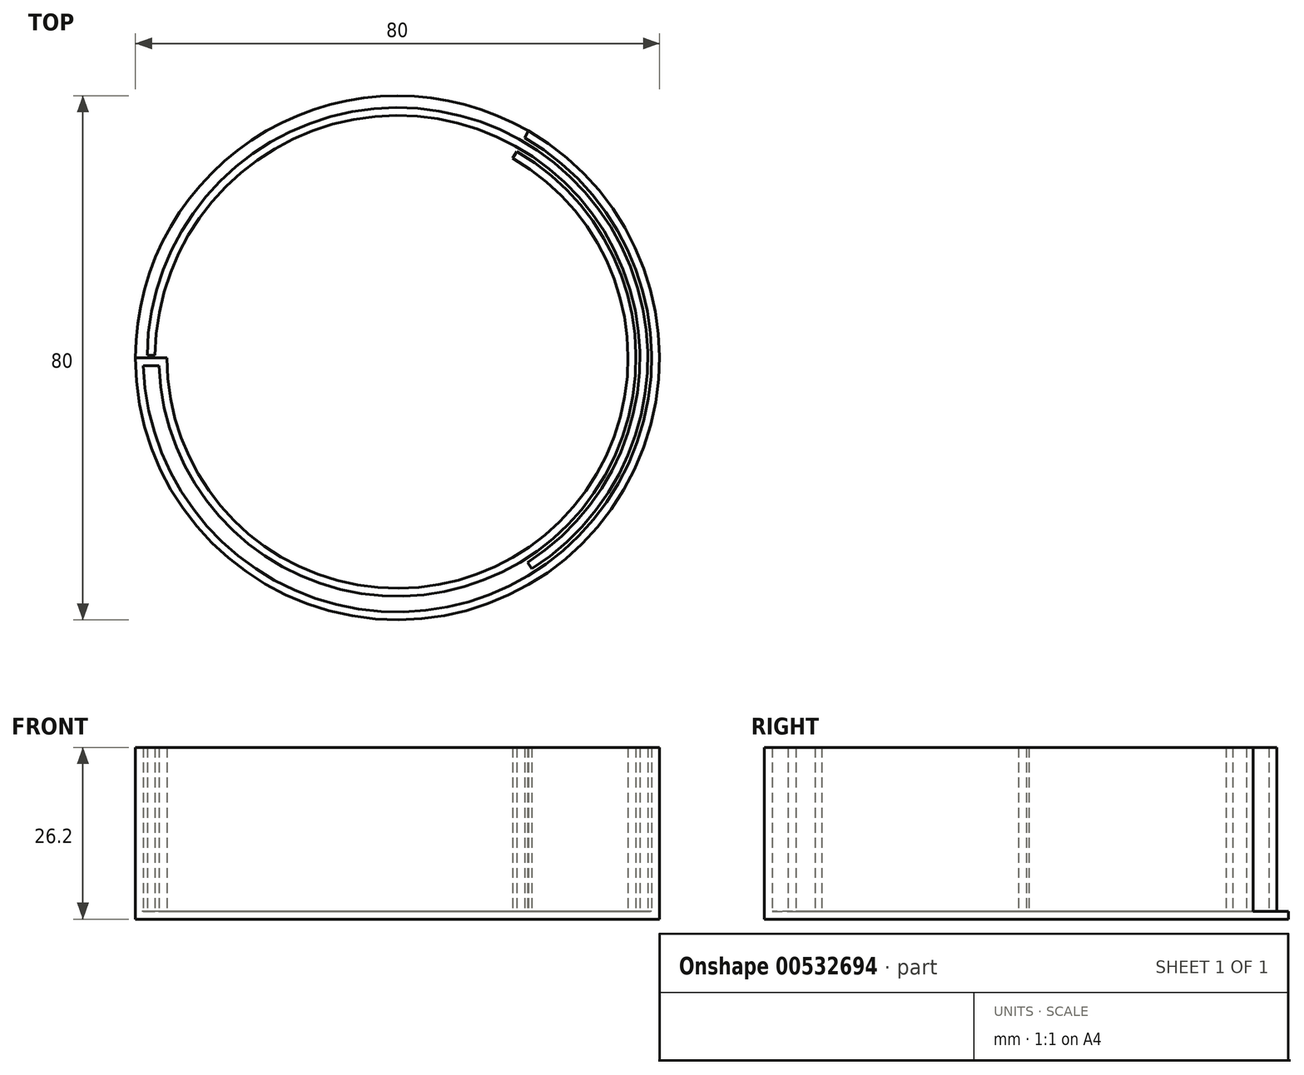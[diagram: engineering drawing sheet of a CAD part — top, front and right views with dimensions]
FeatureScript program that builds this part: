
annotation { "Feature Type Name" : "Feature", "Feature Type Description" : "" }
export const myFeature = defineFeature(function(context is Context, id is Id, definition is map)
    precondition{}
    {
        {
            var Q0;
            Q0=qCreatedBy(makeId("Top.planeOp"),FACE);
            var sketch = newSketch(context, id + "F0", { "sketchPlane" : qUnion([Q0])});
            skCircle(sketch, "E0", {"center": v(0, 0) * mm, "radius": 40 * mm});
            skArc(sketch, "E1", {"start": v(40, -40) * mm, "mid": v(33.16, -34.83) * mm, "end": v(25.67, -30.68) * mm});
            skArc(sketch, "E2", {"start": v(26.28, -40) * mm, "mid": v(21.97, -37.79) * mm, "end": v(17.48, -35.98) * mm});
            skLineSegment(sketch, "E3", {"start": v(-40, -40) * mm, "end": v(-26.28, -40) * mm});
            skArc(sketch, "E4", {"start": v(25.67, -30.68) * mm, "mid": v(0, -25) * mm, "end": v(-25.67, -30.68) * mm, "construction": true});
            skArc(sketch, "E5", {"start": v(17.48, -35.98) * mm, "mid": v(0, -33) * mm, "end": v(-17.48, -35.98) * mm, "construction": true});
            skArc(sketch, "E6", {"start": v(-25.67, -30.68) * mm, "mid": v(-33.16, -34.83) * mm, "end": v(-40, -40) * mm});
            skArc(sketch, "E7", {"start": v(-17.48, -35.98) * mm, "mid": v(-21.97, -37.79) * mm, "end": v(-26.28, -40) * mm});
            skLineSegment(sketch, "E8", {"start": v(26.28, -40) * mm, "end": v(40, -40) * mm});
            skLineSegment(sketch, "E9", {"start": v(-26.28, -40) * mm, "end": v(26.28, -40) * mm, "construction": true});
            skSolve(sketch);
        }
        {
            var Q0;
            {var subQ0=sQuery(id+"F0.wireOp",EDGE,"E0");var subQ1=makeQuery(id+"F0.imprint","INTERSECT",VERTEX,{"derivedFrom":[subQ0,sQuery(id+"F0.wireOp",EDGE,"E6")]});Q0=makeQuery(id+"F0.imprint","IMPRINT",FACE,{"disambiguationData":[TD([[makeQuery(id+"F0.imprint","IMPRINT",EDGE,{"disambiguationData":[TD([[subQ1,-1.0]])],"derivedFrom":subQ0}),1.0]])]});}
            extrude(context, id + "F1", {"entities" : qUnion([Q0]), "depth" : 1.2 * mm, "offsetDistance" : 25 * mm});
        }
        {
            var Q0;
            Q0=makeQuery(id+"F1.opExtrude","CAP_FACE",FACE,{"disambiguationData":[OSD([sQuery(id+"F0.wireOp",EDGE,"E0")])],"isStart":false});
            var sketch = newSketch(context, id + "F2", { "sketchPlane" : qUnion([Q0])});
            skCircle(sketch, "E10", {"center": v(0, 0) * mm, "radius": 40 * mm});
            skCircle(sketch, "E11", {"center": v(0, 0) * mm, "radius": 38.8 * mm});
            skCircle(sketch, "E12", {"center": v(0, 0) * mm, "radius": 36.4 * mm});
            skCircle(sketch, "E13", {"center": v(0, 0) * mm, "radius": 35.2 * mm});
            skLineSegment(sketch, "E14", {"start": v(0, 0) * mm, "end": v(-40, 0) * mm});
            skLineSegment(sketch, "E15", {"start": v(0, 0) * mm, "end": v(20, 34.64) * mm});
            skLineSegment(sketch, "E16", {"start": v(0, 0) * mm, "end": v(20, -34.64) * mm});
            skArc(sketch, "E17", {"start": v(-38.2, 0.41) * mm, "mid": v(18.56, 33.39) * mm, "end": v(20.51, -32.23) * mm});
            skArc(sketch, "E18", {"start": v(-37, 0.4) * mm, "mid": v(17.98, 32.34) * mm, "end": v(19.87, -31.21) * mm});
            skLineSegment(sketch, "E19", {"start": v(-38.2, 0.41) * mm, "end": v(-37, 0.4) * mm});
            skLineSegment(sketch, "E20", {"start": v(19.87, -31.21) * mm, "end": v(20.51, -32.23) * mm});
            skLineSegment(sketch, "E21", {"start": v(-36.38, -1.2) * mm, "end": v(-38.78, -1.2) * mm});
            skSolve(sketch);
        }
        {
            var Q0;
            {var subQ0=sQuery(id+"F2.wireOp",EDGE,"E15");var subQ1=sQuery(id+"F2.wireOp",EDGE,"E10");var subQ2=makeQuery(id+"F2.imprint","INTERSECT",VERTEX,{"derivedFrom":[subQ1,subQ0]});Q0=makeQuery(id+"F2.imprint","IMPRINT",FACE,{"disambiguationData":[TD([[makeQuery(id+"F2.imprint","IMPRINT",EDGE,{"disambiguationData":[TD([[subQ2,1.0]])],"derivedFrom":subQ1}),1.0]])]});}
            var Q1;
            {var subQ0=sQuery(id+"F2.wireOp",EDGE,"E14");var subQ1=sQuery(id+"F2.wireOp",EDGE,"E10");var subQ2=makeQuery(id+"F2.imprint","INTERSECT",VERTEX,{"derivedFrom":[subQ1,subQ0]});Q1=makeQuery(id+"F2.imprint","IMPRINT",FACE,{"disambiguationData":[TD([[makeQuery(id+"F2.imprint","IMPRINT",EDGE,{"disambiguationData":[TD([[subQ2,-1.0]])],"derivedFrom":subQ1}),1.0]])]});}
            var Q2;
            {var subQ5=sQuery(id+"F2.wireOp",EDGE,"E19");Q2=makeQuery(id+"F2.imprint","IMPRINT",FACE,{"disambiguationData":[TD([[makeQuery(id+"F2.imprint","IMPRINT",EDGE,{"derivedFrom":subQ5}),1.0]])]});}
            var Q3;
            {var subQ5=sQuery(id+"F2.wireOp",EDGE,"E20");Q3=makeQuery(id+"F2.imprint","IMPRINT",FACE,{"disambiguationData":[TD([[makeQuery(id+"F2.imprint","IMPRINT",EDGE,{"derivedFrom":subQ5}),1.0]])]});}
            var Q4;
            {var subQ0=sQuery(id+"F2.wireOp",EDGE,"E15");var subQ1=sQuery(id+"F2.wireOp",EDGE,"E12");var subQ2=makeQuery(id+"F2.imprint","INTERSECT",VERTEX,{"derivedFrom":[subQ1,subQ0]});Q4=makeQuery(id+"F2.imprint","IMPRINT",FACE,{"disambiguationData":[TD([[makeQuery(id+"F2.imprint","IMPRINT",EDGE,{"disambiguationData":[TD([[subQ2,1.0]])],"derivedFrom":subQ1}),1.0]])]});}
            var Q5;
            {var subQ0=sQuery(id+"F2.wireOp",EDGE,"E14");var subQ1=sQuery(id+"F2.wireOp",EDGE,"E12");var subQ2=makeQuery(id+"F2.imprint","INTERSECT",VERTEX,{"derivedFrom":[subQ1,subQ0]});Q5=makeQuery(id+"F2.imprint","IMPRINT",FACE,{"disambiguationData":[TD([[makeQuery(id+"F2.imprint","IMPRINT",EDGE,{"disambiguationData":[TD([[subQ2,-1.0]])],"derivedFrom":subQ1}),1.0]])]});}
            var Q6;
            {var subQ0=sQuery(id+"F2.wireOp",EDGE,"E21");Q6=makeQuery(id+"F2.imprint","IMPRINT",FACE,{"disambiguationData":[TD([[makeQuery(id+"F2.imprint","IMPRINT",EDGE,{"derivedFrom":subQ0}),-1.0]])]});}
            extrude(context, id + "F3", {"entities" : qUnion([Q0, Q1, Q2, Q3, Q4, Q5, Q6]), "operationType" : NewBodyOperationType.ADD, "depth" : 25 * mm, "offsetDistance" : 25 * mm});
        }
    });
